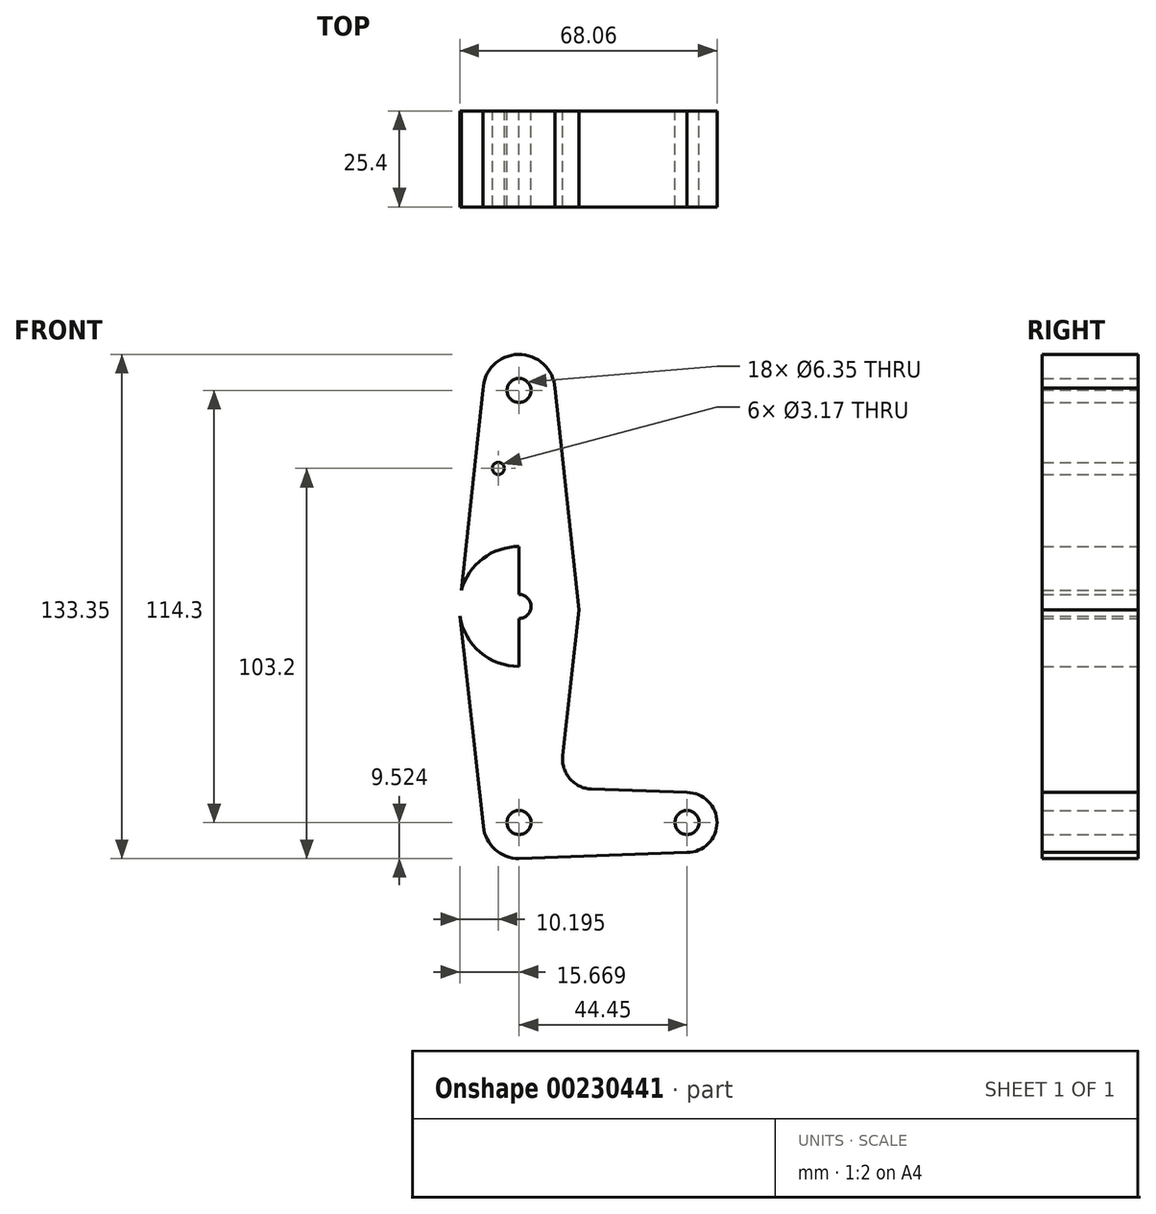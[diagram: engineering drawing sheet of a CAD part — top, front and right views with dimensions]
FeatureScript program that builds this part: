
annotation { "Feature Type Name" : "Feature", "Feature Type Description" : "" }
export const myFeature = defineFeature(function(context is Context, id is Id, definition is map)
    precondition{}
    {
        {
            var Q0;
            Q0=qCreatedBy(makeId("Front.planeOp"),FACE);
            var sketch = newSketch(context, id + "F0", { "sketchPlane" : qUnion([Q0])});
            skLineSegment(sketch, "E0", {"start": v(-35.45, 73.85) * mm, "end": v(-35.45, -40.45) * mm});
            skLineSegment(sketch, "E1", {"start": v(-35.45, -40.45) * mm, "end": v(9, -40.45) * mm});
            skCircle(sketch, "E2", {"center": v(-35.45, 73.85) * mm, "radius": 9.53 * mm});
            skCircle(sketch, "E3", {"center": v(-35.45, 16.7) * mm, "radius": 15.88 * mm});
            skCircle(sketch, "E4", {"center": v(-35.45, -40.45) * mm, "radius": 9.53 * mm});
            skCircle(sketch, "E5", {"center": v(9, -40.45) * mm, "radius": 7.94 * mm});
            skLineSegment(sketch, "E6", {"start": v(-44.97, 74) * mm, "end": v(-51.3, 15.77) * mm});
            skLineSegment(sketch, "E7", {"start": v(-25.95, 74.46) * mm, "end": v(-19.6, 15.77) * mm});
            skLineSegment(sketch, "E8", {"start": v(-51.3, 15.77) * mm, "end": v(-44.92, -41.5) * mm});
            skLineSegment(sketch, "E9", {"start": v(-19.6, 15.77) * mm, "end": v(-23.9, -22.78) * mm});
            skLineSegment(sketch, "E10", {"start": v(-16.28, -31.6) * mm, "end": v(9, -32.5) * mm});
            skLineSegment(sketch, "E11", {"start": v(-35.45, -49.97) * mm, "end": v(9, -48.38) * mm});
            skLineSegment(sketch, "E12", {"start": v(-35.45, 16.7) * mm, "end": v(-35.45, -40.45) * mm});
            skCircle(sketch, "E13", {"center": v(-40.93, 53.23) * mm, "radius": 1.59 * mm});
            skCircle(sketch, "E14", {"center": v(-35.45, 73.85) * mm, "radius": 3.18 * mm});
            skCircle(sketch, "E15", {"center": v(-35.45, 16.7) * mm, "radius": 3.18 * mm});
            skCircle(sketch, "E16", {"center": v(-35.45, -40.45) * mm, "radius": 3.18 * mm});
            skCircle(sketch, "E17", {"center": v(9, -40.45) * mm, "radius": 3.18 * mm});
            skPoint(sketch, "E18.newPointB", {"position": v(-25.98, -41.5) * mm});
            skArc(sketch, "E18.filletArc", {"start": v(-23.9, -22.78) * mm, "mid": v(-22.02, -28.85) * mm, "end": v(-16.28, -31.6) * mm});
            skSolve(sketch);
        }
        {
            var Q0;
            Q0=makeQuery(id+"F0.imprint","IMPRINT",FACE,{"disambiguationData":[TD([[makeQuery(id+"F0.imprint","IMPRINT",EDGE,{"derivedFrom":sQuery(id+"F0.wireOp",EDGE,"E14")}),-1.0]])]});
            var Q1;
            {var subQ0=sQuery(id+"F0.wireOp",EDGE,"E2");var subQ1=sQuery(id+"F0.wireOp",EDGE,"E0");var subQ2=makeQuery(id+"F0.imprint","INTERSECT",VERTEX,{"derivedFrom":[subQ1,subQ0]});Q1=makeQuery(id+"F0.imprint","IMPRINT",FACE,{"disambiguationData":[TD([[makeQuery(id+"F0.imprint","IMPRINT",EDGE,{"disambiguationData":[TD([[subQ2,-1.0]])],"derivedFrom":subQ1}),1.0]])]});}
            var Q2;
            Q2=makeQuery(id+"F0.imprint","IMPRINT",FACE,{"disambiguationData":[TD([[makeQuery(id+"F0.imprint","IMPRINT",EDGE,{"derivedFrom":sQuery(id+"F0.wireOp",EDGE,"E13")}),-1.0]])]});
            var Q3;
            {var subQ2=sQuery(id+"F0.wireOp",EDGE,"E3");var subQ5=sQuery(id+"F0.wireOp",EDGE,"E0");var subQ6=makeQuery(id+"F0.imprint","INTERSECT",VERTEX,{"derivedFrom":[subQ5,subQ2]});Q3=makeQuery(id+"F0.imprint","IMPRINT",FACE,{"disambiguationData":[TD([[makeQuery(id+"F0.imprint","IMPRINT",EDGE,{"disambiguationData":[TD([[subQ6,-1.0]])],"derivedFrom":subQ5}),1.0]])]});}
            var Q4;
            {var subQ1=sQuery(id+"F0.wireOp",EDGE,"E3");var subQ10=sQuery(id+"F0.wireOp",EDGE,"E0");var subQ11=makeQuery(id+"F0.imprint","INTERSECT",VERTEX,{"derivedFrom":[subQ10,subQ1]});Q4=makeQuery(id+"F0.imprint","IMPRINT",FACE,{"disambiguationData":[TD([[makeQuery(id+"F0.imprint","IMPRINT",EDGE,{"disambiguationData":[TD([[subQ11,-1.0]])],"derivedFrom":subQ10}),-1.0]])]});}
            var Q5;
            {var subQ0=sQuery(id+"F0.wireOp",EDGE,"E8");var subQ1=sQuery(id+"F0.wireOp",EDGE,"E3");var subQ2=makeQuery(id+"F0.imprint","INTERSECT",VERTEX,{"derivedFrom":[subQ1,subQ0]});Q5=makeQuery(id+"F0.imprint","IMPRINT",FACE,{"disambiguationData":[TD([[makeQuery(id+"F0.imprint","IMPRINT",EDGE,{"disambiguationData":[TD([[subQ2,-1.0]])],"derivedFrom":subQ1}),-1.0]])]});}
            var Q6;
            {var subQ10=sQuery(id+"F0.wireOp",EDGE,"E10");Q6=makeQuery(id+"F0.imprint","IMPRINT",FACE,{"disambiguationData":[TD([[makeQuery(id+"F0.imprint","IMPRINT",EDGE,{"derivedFrom":subQ10}),-1.0]])]});}
            var Q7;
            {var subQ0=sQuery(id+"F0.wireOp",EDGE,"E16");var subQ1=sQuery(id+"F0.wireOp",EDGE,"E1");var subQ2=makeQuery(id+"F0.imprint","INTERSECT",VERTEX,{"derivedFrom":[subQ1,subQ0]});Q7=makeQuery(id+"F0.imprint","IMPRINT",FACE,{"disambiguationData":[TD([[makeQuery(id+"F0.imprint","IMPRINT",EDGE,{"disambiguationData":[TD([[subQ2,-1.0]])],"derivedFrom":subQ1}),1.0]])]});}
            var Q8;
            {var subQ4=sQuery(id+"F0.wireOp",EDGE,"E16");var subQ8=sQuery(id+"F0.wireOp",EDGE,"E1");var subQ10=makeQuery(id+"F0.imprint","INTERSECT",VERTEX,{"derivedFrom":[subQ8,subQ4]});Q8=makeQuery(id+"F0.imprint","IMPRINT",FACE,{"disambiguationData":[TD([[makeQuery(id+"F0.imprint","IMPRINT",EDGE,{"disambiguationData":[TD([[subQ10,-1.0]])],"derivedFrom":subQ8}),-1.0]])]});}
            var Q9;
            {var subQ0=sQuery(id+"F0.wireOp",EDGE,"E5");var subQ1=sQuery(id+"F0.wireOp",EDGE,"E1");var subQ2=makeQuery(id+"F0.imprint","INTERSECT",VERTEX,{"derivedFrom":[subQ1,subQ0]});Q9=makeQuery(id+"F0.imprint","IMPRINT",FACE,{"disambiguationData":[TD([[makeQuery(id+"F0.imprint","IMPRINT",EDGE,{"disambiguationData":[TD([[subQ2,1.0]])],"derivedFrom":subQ1}),-1.0]])]});}
            var Q10;
            Q10=makeQuery(id+"F0.imprint","IMPRINT",FACE,{"disambiguationData":[TD([[makeQuery(id+"F0.imprint","IMPRINT",EDGE,{"derivedFrom":sQuery(id+"F0.wireOp",EDGE,"E17")}),-1.0]])]});
            extrude(context, id + "F1", {"entities" : qUnion([Q0, Q1, Q2, Q3, Q4, Q5, Q6, Q7, Q8, Q9, Q10]), "depth" : 25.4 * mm});
        }
    });
